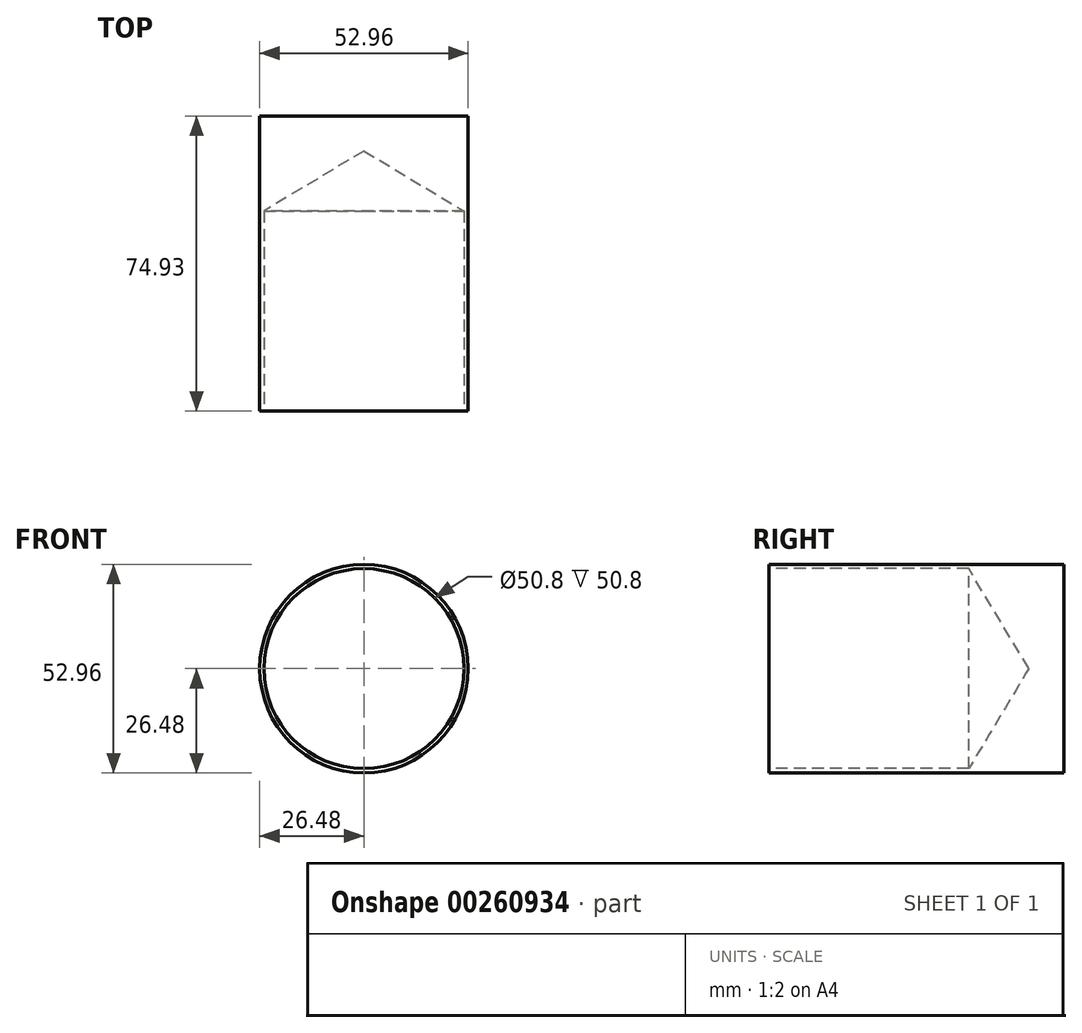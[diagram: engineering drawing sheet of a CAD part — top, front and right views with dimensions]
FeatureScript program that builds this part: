
annotation { "Feature Type Name" : "Feature", "Feature Type Description" : "" }
export const myFeature = defineFeature(function(context is Context, id is Id, definition is map)
    precondition{}
    {
        {
            var Q0;
            Q0=qCreatedBy(makeId("Front.planeOp"),FACE);
            var sketch = newSketch(context, id + "F0", { "sketchPlane" : qUnion([Q0])});
            skCircle(sketch, "E0", {"center": v(0, 0) * mm, "radius": 26.48 * mm});
            skSolve(sketch);
        }
        {
            var Q0;
            Q0 = qSketchRegion(id + "F0", true);
            extrude(context, id + "F1", {"entities" : qUnion([Q0]), "depth" : 74.93 * mm});
        }
        {
            var Q0;
            Q0=makeQuery(id+"F1.opExtrude","CAP_FACE",FACE,{"disambiguationData":[OSD([sQuery(id+"F0.wireOp",EDGE,"E0")])],"isStart":false});
            var sketch = newSketch(context, id + "F2", { "sketchPlane" : qUnion([Q0])});
            skLineSegment(sketch, "E1.bottom", {"start": v(0, 0) * mm, "end": v(4.24, 0) * mm});
            skLineSegment(sketch, "E1.top", {"start": v(0, 3.18) * mm, "end": v(4.24, 3.18) * mm});
            skLineSegment(sketch, "E1.left", {"start": v(0, 0) * mm, "end": v(0, 3.18) * mm});
            skLineSegment(sketch, "E1.right", {"start": v(4.24, 0) * mm, "end": v(4.24, 3.18) * mm});
            skSolve(sketch);
        }
        {
            var Q0;
            Q0=sQuery(id+"F2.wireOp",VERTEX,"E1.left.start");
            var Q1;
            Q1=makeQuery(id+"F1.opExtrude","SWEPT_BODY",BODY,{"disambiguationData":[OSD([sQuery(id+"F0.wireOp",EDGE,"E0")])]});
            hole(context, id + "F3", {"style" : HoleStyle.SIMPLE, "endStyle" : HoleEndStyle.BLIND, "holeDiameter" : 50.8 * mm, "holeDepth" : 50.8 * mm, "tappedDepth" : 12.7 * mm, "tapClearance" : 3, "locations" : qUnion([Q0]), "scope" : qUnion([Q1])});
        }
    });
